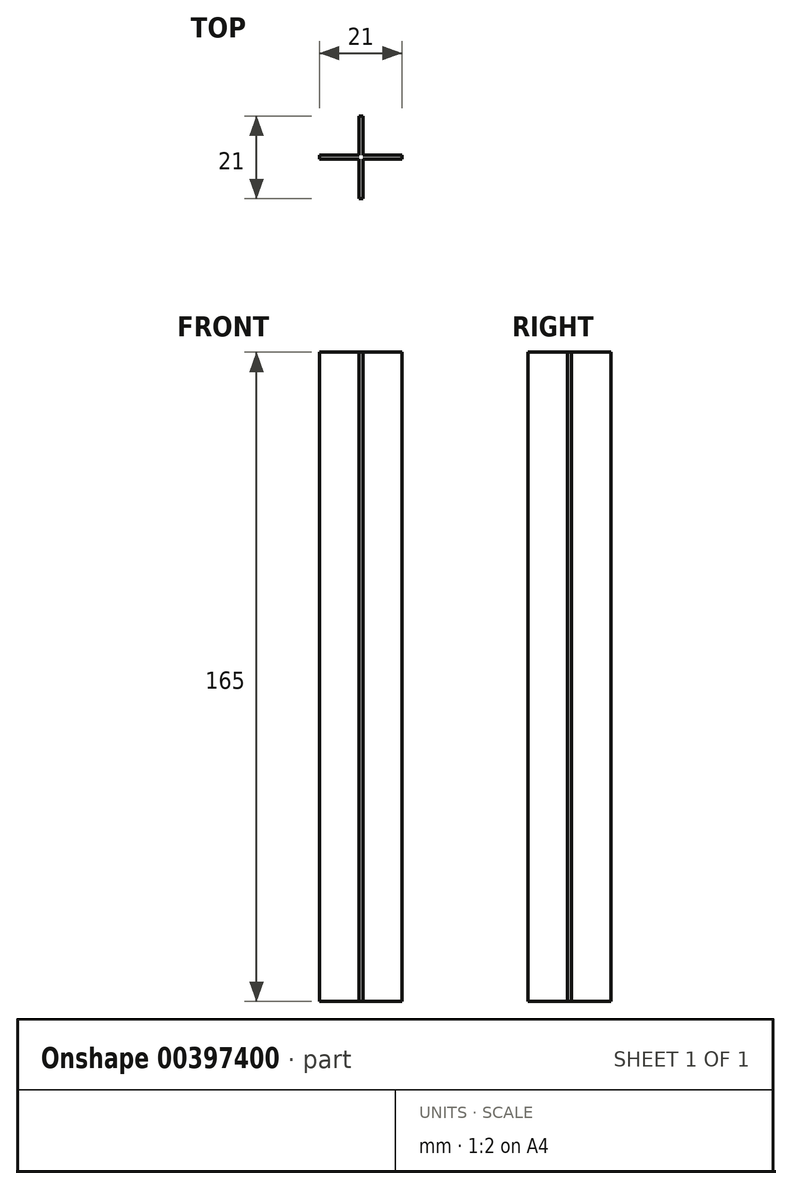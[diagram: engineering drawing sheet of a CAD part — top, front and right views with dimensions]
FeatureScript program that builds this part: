
annotation { "Feature Type Name" : "Feature", "Feature Type Description" : "" }
export const myFeature = defineFeature(function(context is Context, id is Id, definition is map)
    precondition{}
    {
        {
            var Q0;
            Q0=qCreatedBy(makeId("Top.planeOp"),FACE);
            var sketch = newSketch(context, id + "F0", { "sketchPlane" : qUnion([Q0])});
            skLineSegment(sketch, "E0", {"start": v(0, 0) * mm, "end": v(-10, 0) * mm});
            skLineSegment(sketch, "E1", {"start": v(-10, 0) * mm, "end": v(-10, -1) * mm});
            skLineSegment(sketch, "E2", {"start": v(-10, -1) * mm, "end": v(0, -1) * mm});
            skLineSegment(sketch, "E3", {"start": v(0, -1) * mm, "end": v(0, -11) * mm});
            skLineSegment(sketch, "E4", {"start": v(0, -11) * mm, "end": v(1, -11) * mm});
            skLineSegment(sketch, "E5", {"start": v(1, -11) * mm, "end": v(1, -1) * mm});
            skLineSegment(sketch, "E6", {"start": v(1, -1) * mm, "end": v(11, -1) * mm});
            skLineSegment(sketch, "E7", {"start": v(11, -1) * mm, "end": v(11, 0) * mm});
            skLineSegment(sketch, "E8", {"start": v(11, 0) * mm, "end": v(1, 0) * mm});
            skLineSegment(sketch, "E9", {"start": v(1, 0) * mm, "end": v(1, 10) * mm});
            skLineSegment(sketch, "E10", {"start": v(1, 10) * mm, "end": v(0, 10) * mm});
            skLineSegment(sketch, "E11", {"start": v(0, 10) * mm, "end": v(0, 0) * mm});
            skSolve(sketch);
        }
        {
            var Q0;
            Q0=makeQuery(id+"F0.imprint","IMPRINT",FACE,{"disambiguationData":[TD([[makeQuery(id+"F0.imprint","IMPRINT",EDGE,{"derivedFrom":sQuery(id+"F0.wireOp",EDGE,"E0")}),1.0]])]});
            extrude(context, id + "F1", {"entities" : qUnion([Q0]), "depth" : 165 * mm});
        }
    });
